# Revit family: Basin-Vessel-DXV-Pop_Rectangle-D20080022_Series
name_source: partatom
category: Plumbing Fixtures
revit_build: Autodesk Revit 2014 (Build: 20130308_1515(x64)
units: mm (PartAtom-declared; Revit-internal decimal feet)

## types (5) — shared parameters
Assembly Code = D2010310
Basin Shape = Rectangular
CW Connection = Yes
CWFU = 1.5
Cold Water Connection Diameter = 1/2"
Cold Water Connection Height = 20"
Cold Water Connection Radius = 1/4"
Cold Water Connection Width = 3"
Default Elevation = 28"
Description = Pop Rectangle Vessel Lavatory
HW Connection = Yes
HWFU = 1.5
Height = 5"
Hot Water Connection Diameter = 1/2"
Hot Water Connection Height = 20"
Hot Water Connection Radius = 1/4"
Hot Water Connection Width = 3"
Installation Type = Above Counter
Length = 15"
Manufacturer = DXV
Outlet Location = 4"
Price = Prices may vary. Please consult Manufacturer Rep for most up-to-date price list.
Product Documentation Link = https://dxv01.blob.core.windows.net
Product Page URL = https://www.dxv.com
URL = https://www.dxv.com
Vent Connection = No
WFU = 2
Warranty Documentation Link = https://www.dxv.com
Waste Connection = Yes
Waste Connection Diameter = 1 1/4"
Waste Connection Height = 18"
Waste Connection Radius = 5/8"
Width = 15"

## per-type parameters (varying)
| type | Finish | Material |
| D20080022.415 | Fine Fire Clay-DXV-415-Canvas White | Fine Fire Clay-DXV-415-Canvas White |
| D20080022.059 | Fine Fire Clay-DXV-059-Matte Black | Fine Fire Clay-DXV-059-Matte Black |
| D20080022.178 | Fine Fire Clay-DXV-178-Black | Fine Fire Clay-DXV-178-Black |
| D20080022.405 | Fine Fire Clay-DXV-405-Pearlescent White | Fine Fire Clay-DXV-405-Pearlescent White |
| D20080022.425 | Fine Fire Clay-DXV-425-Chenille Gray | Fine Fire Clay-DXV-425-Chenille Gray |

note: column(s) folded — value = type name in every type: Model

## geometry (parser evidence)
native form markers: Sweep x1
no freeform markers — native parametric forms only
